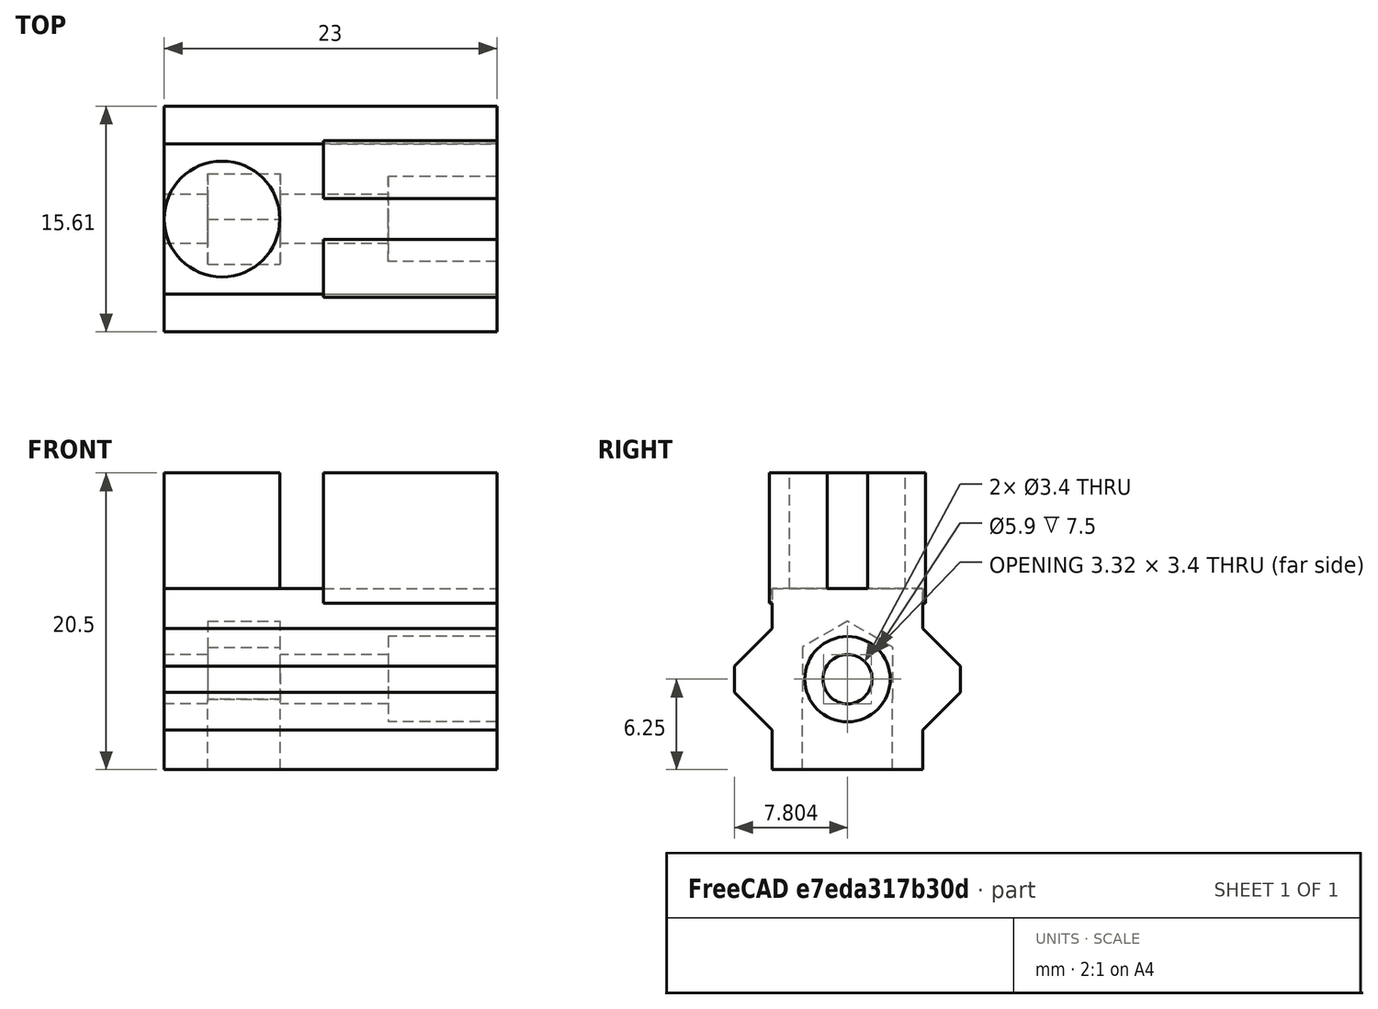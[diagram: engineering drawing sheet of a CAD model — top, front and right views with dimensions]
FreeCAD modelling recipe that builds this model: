
FCSTD DOCUMENT  (FreeCAD 0.17R13541 (Git))
Label: Abrazaderas de correa
License: All rights reserved
LicenseURL: http://en.wikipedia.org/wiki/All_rights_reserved
objects: Part::Box×3, Part::Cylinder×3, Part::MultiFuse×3, Part::Polygon×1, Part::Extrusion×1, Part::Prism×1, Part::Cut×1
note: 13 computed .brp shape members not serialized (recipe doc carries the construction recipe); baked Part::Feature solids carry a one-line shape summary decoded from their .brp

FEATURE [Part::Polygon] gt2clamp0base_plane_yz
  Close = true
  Nodes = (12) [(0,2.80417,0),(0,2.80417,2.74375),(0,0.2,5.34792),(0,0.2,7.15208),(0,2.80417,9.75625),(0,2.80417,12.5),(0,13.2042,12.5),(0,13.2042,9.75625),+4 more]
FEATURE [Part::Extrusion] gt2clamp0extr_base
  Base = -> gt2clamp0base_plane_yz
  Dir = (23,0,0)
  DirMode = 0
  FaceMakerClass = Part::FaceMakerExtrusion
  LengthFwd = 0
  LengthRev = 0
  Solid = true
  Symmetric = false
FEATURE [Part::Box] gt2clamp0_cb1
  AttacherType = Attacher::AttachEngine3D
  Height = 9
  Length = 12
  Placement = pos=(11,2.60417,11.5) rot=(0,0,1;0rad)
  Width = 4
FEATURE [Part::Box] gt2clamp0_cb3
  AttacherType = Attacher::AttachEngine3D
  Height = 9
  Length = 12
  Placement = pos=(11,9.40417,11.5) rot=(0,0,1;0rad)
  Width = 4
FEATURE [Part::Prism] gt2clamp0_base_lscrew_nut
  AttacherType = Attacher::AttachEngine3D
  Circumradius = 3.605
  Height = 5.04
  Placement = pos=(3,8.00417,6.65) rot=(0,1,0;1.5708rad)
  Polygon = 6
FEATURE [Part::Cylinder] gt2clamp0_cyl
  Angle = 360
  AttacherType = Attacher::AttachEngine3D
  Height = 9
  Placement = pos=(4,8.00417,11.5) rot=(0,0,1;0rad)
  Radius = 4
FEATURE [Part::MultiFuse] gt2clamp0clamp_base
  Shapes = -> [gt2clamp0_cb1,gt2clamp0_cb3,gt2clamp0_cyl,gt2clamp0extr_base]
FEATURE [Part::Box] gt2clamp0_base_lscrew_nut2
  AttacherType = Attacher::AttachEngine3D
  Height = 6.65
  Length = 5.04
  Placement = pos=(3,4.88224,0) rot=(0,0,1;0rad)
  Width = 6.24386
FEATURE [Part::Cylinder] gt2clamp0_base_lscrew_head
  Angle = 360
  AttacherType = Attacher::AttachEngine3D
  Height = 8.5
  Placement = pos=(0,0,-1) rot=(0,0,1;0rad)
  Radius = 2.95
FEATURE [Part::Cylinder] gt2clamp0_base_lscrew_shank
  Angle = 360
  AttacherType = Attacher::AttachEngine3D
  Height = 25
  Placement = pos=(0,0,-1) rot=(0,0,1;0rad)
  Radius = 1.7
FEATURE [Part::MultiFuse] gt2clamp0_base_lscrew
  Placement = pos=(23,8.00417,6.25) rot=(0,-1,0;1.5708rad)
  Shapes = -> [gt2clamp0_base_lscrew_shank,gt2clamp0_base_lscrew_head]
FEATURE [Part::MultiFuse] gt2clamp0_clamp_hole
  Shapes = -> [gt2clamp0_base_lscrew,gt2clamp0_base_lscrew_nut,gt2clamp0_base_lscrew_nut2]
FEATURE [Part::Cut] gt2clamp0
  Base = -> gt2clamp0clamp_base
  Placement = pos=(100,1.2,12.5) rot=(0,0,1;0rad)
  Tool = -> gt2clamp0_clamp_hole
